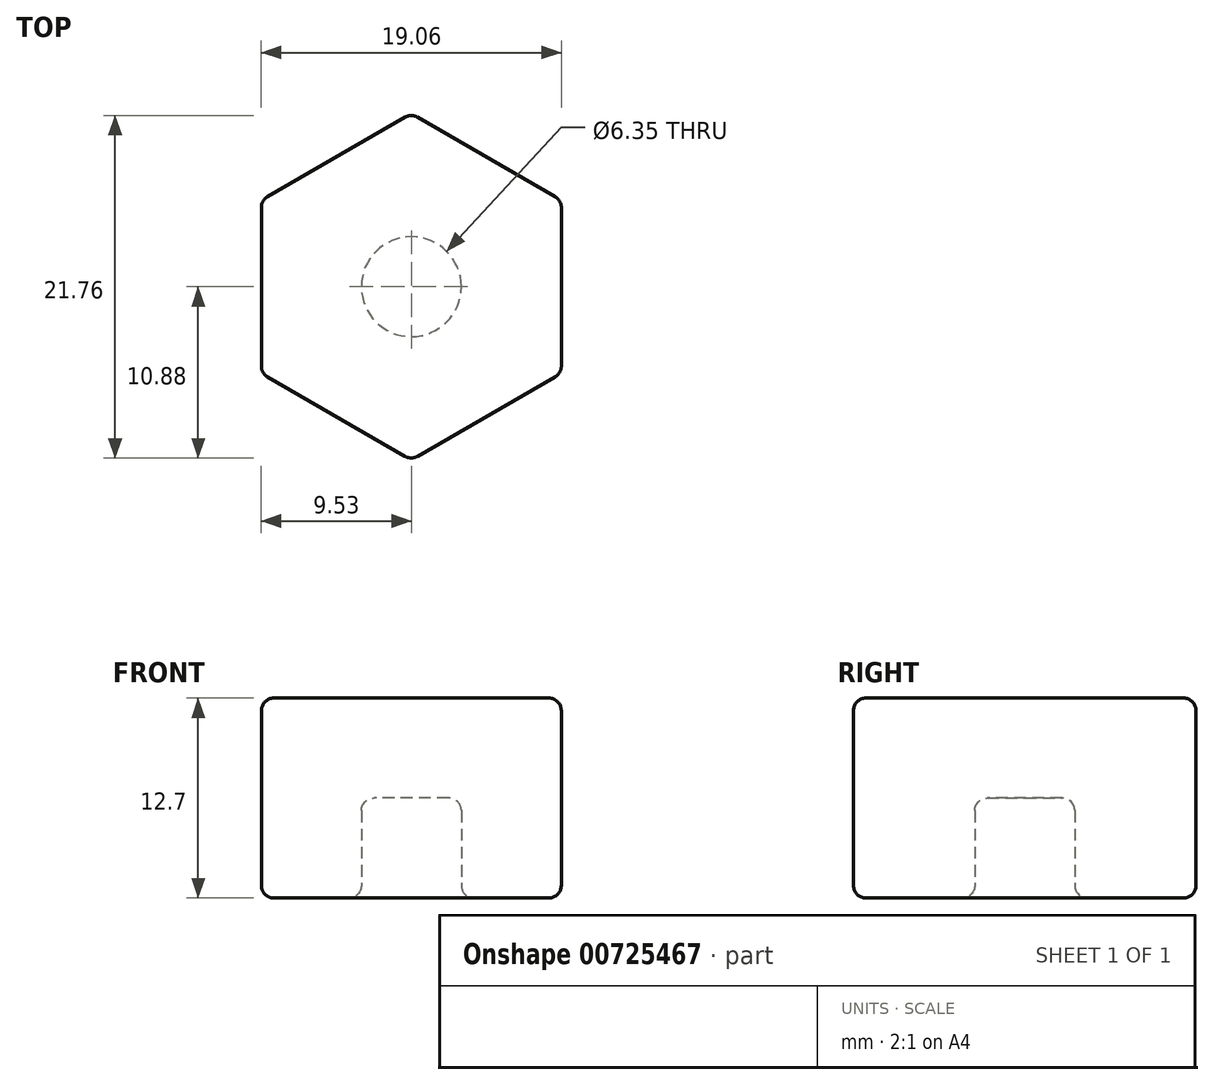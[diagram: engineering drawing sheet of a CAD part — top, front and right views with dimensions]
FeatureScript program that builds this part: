
annotation { "Feature Type Name" : "Feature", "Feature Type Description" : "" }
export const myFeature = defineFeature(function(context is Context, id is Id, definition is map)
    precondition{}
    {
        {
            var Q0;
            Q0=qCreatedBy(makeId("Top.planeOp"),FACE);
            var sketch = newSketch(context, id + "F0", { "sketchPlane" : qUnion([Q0])});
            skCircle(sketch, "E0", {"center": v(0, 0) * mm, "radius": 3.18 * mm});
            skCircle(sketch, "E1.cCircle", {"center": v(0, 0) * mm, "radius": 9.53 * mm, "construction": true});
            skLineSegment(sketch, "E1.0", {"start": v(9.53, 5.5) * mm, "end": v(9.53, -5.5) * mm});
            skLineSegment(sketch, "E1.1", {"start": v(9.52, -5.5) * mm, "end": v(0, -11) * mm});
            skLineSegment(sketch, "E1.2", {"start": v(0, -11) * mm, "end": v(-9.52, -5.5) * mm});
            skLineSegment(sketch, "E1.3", {"start": v(-9.53, -5.5) * mm, "end": v(-9.53, 5.5) * mm});
            skLineSegment(sketch, "E1.4", {"start": v(-9.53, 5.5) * mm, "end": v(0, 11) * mm});
            skLineSegment(sketch, "E1.5", {"start": v(0, 11) * mm, "end": v(9.53, 5.5) * mm});
            skPoint(sketch, "E1.0.midPoint", {"position": v(9.53, 0) * mm});
            skSolve(sketch);
        }
        {
            var Q0;
            Q0=makeQuery(id+"F0.imprint","IMPRINT",FACE,{"disambiguationData":[TD([[makeQuery(id+"F0.imprint","IMPRINT",EDGE,{"derivedFrom":sQuery(id+"F0.wireOp",EDGE,"E0")}),-1.0]])]});
            var Q1;
            Q1=makeQuery(id+"F0.imprint","IMPRINT",FACE,{"disambiguationData":[TD([[makeQuery(id+"F0.imprint","IMPRINT",EDGE,{"derivedFrom":sQuery(id+"F0.wireOp",EDGE,"E0")}),1.0]])]});
            extrude(context, id + "F1", {"entities" : qUnion([Q0, Q1]), "depth" : 12.7 * mm, "offsetDistance" : 25.4 * mm});
        }
        {
            var Q0;
            Q0=makeQuery(id+"F0.imprint","IMPRINT",FACE,{"disambiguationData":[TD([[makeQuery(id+"F0.imprint","IMPRINT",EDGE,{"derivedFrom":sQuery(id+"F0.wireOp",EDGE,"E0")}),1.0]])]});
            extrude(context, id + "F2", {"entities" : qUnion([Q0]), "operationType" : NewBodyOperationType.REMOVE, "depth" : 6.35 * mm, "offsetDistance" : 25.4 * mm});
        }
        {
            var Q0;
            Q0=makeQuery(id+"F1.opExtrude","SWEPT_FACE",FACE,{"disambiguationData":[OSD([sQuery(id+"F0.wireOp",EDGE,"E1.4")])]});
            var Q1;
            Q1=makeQuery(id+"F1.opExtrude","SWEPT_FACE",FACE,{"disambiguationData":[OSD([sQuery(id+"F0.wireOp",EDGE,"E1.3")])]});
            var Q2;
            Q2=makeQuery(id+"F1.opExtrude","SWEPT_EDGE",EDGE,{"disambiguationData":[OSD([sQuery(id+"F0.wireOp",EDGE,"E1.4"),sQuery(id+"F0.wireOp",EDGE,"E1.5")])]});
            var Q3;
            Q3=makeQuery(id+"F1.opExtrude","SWEPT_FACE",FACE,{"disambiguationData":[OSD([sQuery(id+"F0.wireOp",EDGE,"E1.2")])]});
            var Q4;
            Q4=makeQuery(id+"F1.opExtrude","SWEPT_FACE",FACE,{"disambiguationData":[OSD([sQuery(id+"F0.wireOp",EDGE,"E1.1")])]});
            var Q5;
            Q5=makeQuery(id+"F1.opExtrude","CAP_FACE",FACE,{"disambiguationData":[OSD([sQuery(id+"F0.wireOp",EDGE,"E1.0"),sQuery(id+"F0.wireOp",EDGE,"E1.1"),sQuery(id+"F0.wireOp",EDGE,"E1.2"),sQuery(id+"F0.wireOp",EDGE,"E1.3"),sQuery(id+"F0.wireOp",EDGE,"E1.4"),sQuery(id+"F0.wireOp",EDGE,"E1.5")])],"isStart":false});
            var Q6;
            Q6=makeQuery(id+"F1.opExtrude","SWEPT_EDGE",EDGE,{"disambiguationData":[OSD([sQuery(id+"F0.wireOp",EDGE,"E1.1"),sQuery(id+"F0.wireOp",EDGE,"E1.2")])]});
            var Q7;
            Q7=makeQuery(id+"F1.opExtrude","SWEPT_EDGE",EDGE,{"disambiguationData":[OSD([sQuery(id+"F0.wireOp",EDGE,"E1.0"),sQuery(id+"F0.wireOp",EDGE,"E1.1")])]});
            var Q8;
            Q8=makeQuery(id+"F1.opExtrude","SWEPT_FACE",FACE,{"disambiguationData":[OSD([sQuery(id+"F0.wireOp",EDGE,"E1.0")])]});
            var Q9;
            Q9=makeQuery(id+"F1.opExtrude","SWEPT_EDGE",EDGE,{"disambiguationData":[OSD([sQuery(id+"F0.wireOp",EDGE,"E1.0"),sQuery(id+"F0.wireOp",EDGE,"E1.5")])]});
            var Q10;
            Q10=makeQuery(id+"F1.opExtrude","CAP_EDGE",EDGE,{"disambiguationData":[OSD([sQuery(id+"F0.wireOp",EDGE,"E1.3")])],"isStart":false});
            var Q11;
            Q11=makeQuery(id+"F1.opExtrude","CAP_EDGE",EDGE,{"disambiguationData":[OSD([sQuery(id+"F0.wireOp",EDGE,"E1.0")])],"isStart":false});
            var Q12;
            Q12=makeQuery(id+"F1.opExtrude","SWEPT_FACE",FACE,{"disambiguationData":[OSD([sQuery(id+"F0.wireOp",EDGE,"E1.5")])]});
            var Q13;
            Q13=makeQuery(id+"F1.opExtrude","CAP_EDGE",EDGE,{"disambiguationData":[OSD([sQuery(id+"F0.wireOp",EDGE,"E1.0")])],"isStart":true});
            var Q14;
            Q14=makeQuery(id+"F1.opExtrude","SWEPT_EDGE",EDGE,{"disambiguationData":[OSD([sQuery(id+"F0.wireOp",EDGE,"E1.3"),sQuery(id+"F0.wireOp",EDGE,"E1.4")])]});
            var Q15;
            Q15=makeQuery(id+"F1.opExtrude","SWEPT_EDGE",EDGE,{"disambiguationData":[OSD([sQuery(id+"F0.wireOp",EDGE,"E1.2"),sQuery(id+"F0.wireOp",EDGE,"E1.3")])]});
            var Q16;
            Q16=makeQuery(id+"F1.opExtrude","CAP_EDGE",EDGE,{"disambiguationData":[OSD([sQuery(id+"F0.wireOp",EDGE,"E1.4")])],"isStart":false});
            var Q17;
            Q17=makeQuery(id+"F1.opExtrude","CAP_EDGE",EDGE,{"disambiguationData":[OSD([sQuery(id+"F0.wireOp",EDGE,"E1.4")])],"isStart":true});
            var Q18;
            Q18=makeQuery(id+"F1.opExtrude","CAP_EDGE",EDGE,{"disambiguationData":[OSD([sQuery(id+"F0.wireOp",EDGE,"E1.1")])],"isStart":true});
            var Q19;
            Q19=makeQuery(id+"F1.opExtrude","CAP_EDGE",EDGE,{"disambiguationData":[OSD([sQuery(id+"F0.wireOp",EDGE,"E1.1")])],"isStart":false});
            var Q20;
            Q20=makeQuery(id+"F1.opExtrude","CAP_EDGE",EDGE,{"disambiguationData":[OSD([sQuery(id+"F0.wireOp",EDGE,"E1.2")])],"isStart":true});
            var Q21;
            Q21=makeQuery(id+"F1.opExtrude","CAP_EDGE",EDGE,{"disambiguationData":[OSD([sQuery(id+"F0.wireOp",EDGE,"E1.2")])],"isStart":false});
            var Q22;
            Q22=makeQuery(id+"F1.opExtrude","CAP_EDGE",EDGE,{"disambiguationData":[OSD([sQuery(id+"F0.wireOp",EDGE,"E1.3")])],"isStart":true});
            var Q23;
            Q23=makeQuery(id+"F1.opExtrude","CAP_EDGE",EDGE,{"disambiguationData":[OSD([sQuery(id+"F0.wireOp",EDGE,"E1.5")])],"isStart":true});
            var Q24;
            Q24=makeQuery(id+"F1.opExtrude","CAP_EDGE",EDGE,{"disambiguationData":[OSD([sQuery(id+"F0.wireOp",EDGE,"E1.5")])],"isStart":false});
            var Q25;
            Q25=makeQuery(id+"F2.boolean.opBoolean","COPY",FACE,{"derivedFrom":makeQuery(id+"F2.opExtrude","SWEPT_FACE",FACE,{"disambiguationData":[OSD([sQuery(id+"F0.wireOp",EDGE,"E0")])]})});
            var Q26;
            Q26=makeQuery(id+"F2.boolean.opBoolean","COPY",EDGE,{"derivedFrom":makeQuery(id+"F2.opExtrude","CAP_EDGE",EDGE,{"disambiguationData":[OSD([sQuery(id+"F0.wireOp",EDGE,"E0")])],"isStart":false})});
            var Q27;
            Q27=makeQuery(id+"F2.boolean.opBoolean","COPY",FACE,{"derivedFrom":makeQuery(id+"F2.opExtrude","CAP_FACE",FACE,{"disambiguationData":[OSD([sQuery(id+"F0.wireOp",EDGE,"E0")])],"isStart":false})});
            var Q28;
            Q28=makeQuery(id+"F1.opExtrude","CAP_FACE",FACE,{"disambiguationData":[OSD([sQuery(id+"F0.wireOp",EDGE,"E1.0"),sQuery(id+"F0.wireOp",EDGE,"E1.1"),sQuery(id+"F0.wireOp",EDGE,"E1.2"),sQuery(id+"F0.wireOp",EDGE,"E1.3"),sQuery(id+"F0.wireOp",EDGE,"E1.4"),sQuery(id+"F0.wireOp",EDGE,"E1.5")])],"isStart":true});
            var Q29;
            Q29=makeQuery(id+"F2.boolean.opBoolean","COPY",EDGE,{"derivedFrom":makeQuery(id+"F2.opExtrude","CAP_EDGE",EDGE,{"disambiguationData":[OSD([sQuery(id+"F0.wireOp",EDGE,"E0")])],"isStart":true})});
            fillet(context, id + "F3", {"entities" : qUnion([Q0, Q1, Q2, Q3, Q4, Q5, Q6, Q7, Q8, Q9, Q10, Q11, Q12, Q13, Q14, Q15, Q16, Q17, Q18, Q19, Q20, Q21, Q22, Q23, Q24, Q25, Q26, Q27, Q28, Q29]), "radius" : 0.8 * mm, "tangentPropagation" : true, "allowEdgeOverflow" : false});
        }
    });
